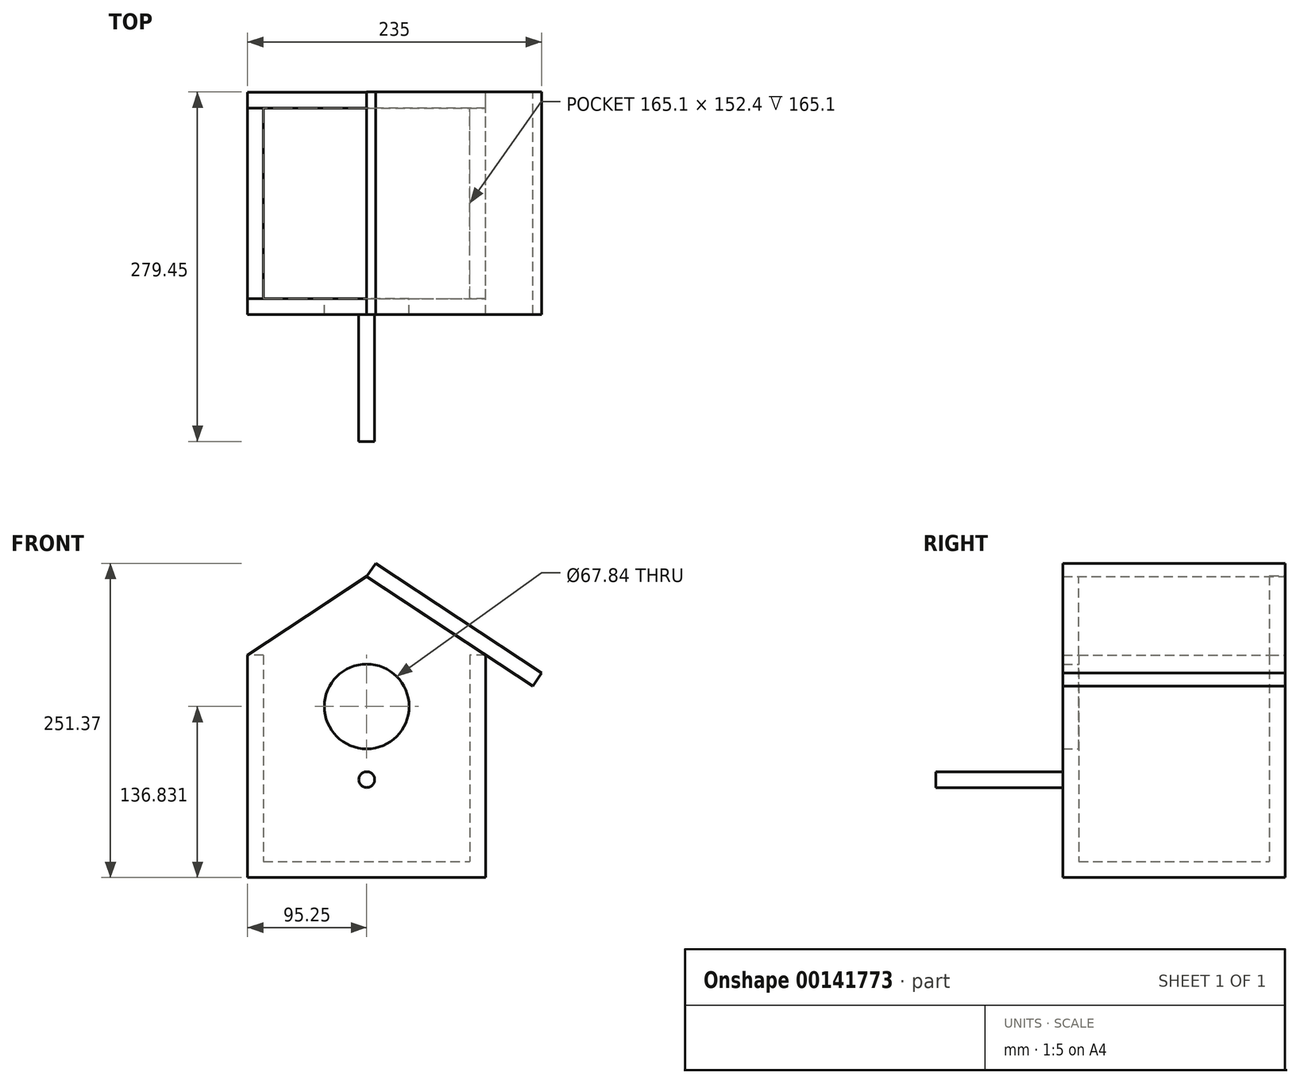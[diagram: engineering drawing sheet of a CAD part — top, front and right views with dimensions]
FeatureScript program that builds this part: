
annotation { "Feature Type Name" : "Feature", "Feature Type Description" : "" }
export const myFeature = defineFeature(function(context is Context, id is Id, definition is map)
    precondition{}
    {
        {
            var Q0;
            Q0=qCreatedBy(makeId("Front.planeOp"),FACE);
            var sketch = newSketch(context, id + "F0", { "sketchPlane" : qUnion([Q0])});
            skLineSegment(sketch, "E0.bottom", {"start": v(-82.55, 82.55) * mm, "end": v(82.55, 82.55) * mm});
            skLineSegment(sketch, "E0.top", {"start": v(-82.55, -82.55) * mm, "end": v(82.55, -82.55) * mm});
            skLineSegment(sketch, "E0.left", {"start": v(-82.55, 82.55) * mm, "end": v(-82.55, -82.55) * mm});
            skLineSegment(sketch, "E0.right", {"start": v(82.55, 82.55) * mm, "end": v(82.55, -82.55) * mm});
            skPoint(sketch, "E0.middle", {"position": v(0, 0) * mm});
            skLineSegment(sketch, "E1", {"start": v(0, 0) * mm, "end": v(0, 145.53) * mm});
            skLineSegment(sketch, "E2", {"start": v(0, 145.53) * mm, "end": v(82.55, 82.55) * mm});
            skLineSegment(sketch, "E3", {"start": v(0, 145.53) * mm, "end": v(-82.55, 82.55) * mm});
            skCircle(sketch, "E4", {"center": v(0, 41.58) * mm, "radius": 33.92 * mm});
            skCircle(sketch, "E5", {"center": v(0, -25.65) * mm, "radius": 12.62 * mm});
            skSolve(sketch);
        }
        {
            var Q0;
            Q0=makeQuery(id+"F0.imprint","IMPRINT",FACE,{"disambiguationData":[TD([[makeQuery(id+"F0.imprint","IMPRINT",EDGE,{"derivedFrom":sQuery(id+"F0.wireOp",EDGE,"E0.top")}),1.0]])]});
            var Q1;
            {var subQ0=sQuery(id+"F0.wireOp",EDGE,"E3");Q1=makeQuery(id+"F0.imprint","IMPRINT",FACE,{"disambiguationData":[TD([[makeQuery(id+"F0.imprint","IMPRINT",EDGE,{"derivedFrom":subQ0}),1.0]])]});}
            var Q2;
            {var subQ0=sQuery(id+"F0.wireOp",EDGE,"E2");Q2=makeQuery(id+"F0.imprint","IMPRINT",FACE,{"disambiguationData":[TD([[makeQuery(id+"F0.imprint","IMPRINT",EDGE,{"derivedFrom":subQ0}),-1.0]])]});}
            var Q3;
            Q3=makeQuery(id+"F0.imprint","IMPRINT",FACE,{"disambiguationData":[TD([[makeQuery(id+"F0.imprint","IMPRINT",EDGE,{"derivedFrom":sQuery(id+"F0.wireOp",EDGE,"E5")}),1.0]])]});
            extrude(context, id + "F1", {"entities" : qUnion([Q0, Q1, Q2, Q3]), "depth" : 12.7 * mm});
        }
        {
            var Q0;
            Q0=makeQuery(id+"F1.opExtrude","CAP_FACE",FACE,{"disambiguationData":[OSD([sQuery(id+"F0.wireOp",EDGE,"E0.top"),sQuery(id+"F0.wireOp",EDGE,"E0.left"),sQuery(id+"F0.wireOp",EDGE,"E0.right"),sQuery(id+"F0.wireOp",EDGE,"E2"),sQuery(id+"F0.wireOp",EDGE,"E3"),sQuery(id+"F0.wireOp",EDGE,"E4")])],"isStart":false});
            var sketch = newSketch(context, id + "F2", { "sketchPlane" : qUnion([Q0])});
            skCircle(sketch, "E6", {"center": v(0, -16.87) * mm, "radius": 6.35 * mm});
            skSolve(sketch);
        }
        {
            var Q0;
            Q0 = qSketchRegion(id + "F2", true);
            extrude(context, id + "F3", {"entities" : qUnion([Q0]), "depth" : 101.6 * mm});
        }
        {
            var Q0;
            Q0=makeQuery(id+"F1.opExtrude","SWEPT_FACE",FACE,{"disambiguationData":[OSD([sQuery(id+"F0.wireOp",EDGE,"E0.right")])]});
            var sketch = newSketch(context, id + "F4", { "sketchPlane" : qUnion([Q0])});
            skLineSegment(sketch, "E7.bottom", {"start": v(-12.7, 82.55) * mm, "end": v(152.4, 82.55) * mm});
            skLineSegment(sketch, "E7.top", {"start": v(-12.7, -82.55) * mm, "end": v(152.4, -82.55) * mm});
            skLineSegment(sketch, "E7.left", {"start": v(-12.7, 82.55) * mm, "end": v(-12.7, -82.55) * mm});
            skLineSegment(sketch, "E7.right", {"start": v(152.4, 82.55) * mm, "end": v(152.4, -82.55) * mm});
            skSolve(sketch);
        }
        {
            var Q0;
            Q0 = qSketchRegion(id + "F4", true);
            extrude(context, id + "F5", {"entities" : qUnion([Q0]), "operationType" : NewBodyOperationType.ADD, "depth" : 12.7 * mm});
        }
        {
            var Q0;
            Q0=makeQuery(id+"F1.opExtrude","SWEPT_FACE",FACE,{"disambiguationData":[OSD([sQuery(id+"F0.wireOp",EDGE,"E0.left")])]});
            var sketch = newSketch(context, id + "F6", { "sketchPlane" : qUnion([Q0])});
            skLineSegment(sketch, "E8.bottom", {"start": v(12.7, 82.55) * mm, "end": v(-152.4, 82.55) * mm});
            skLineSegment(sketch, "E8.top", {"start": v(12.7, -82.55) * mm, "end": v(-152.4, -82.55) * mm});
            skLineSegment(sketch, "E8.left", {"start": v(12.7, 82.55) * mm, "end": v(12.7, -82.55) * mm});
            skLineSegment(sketch, "E8.right", {"start": v(-152.4, 82.55) * mm, "end": v(-152.4, -82.55) * mm});
            skSolve(sketch);
        }
        {
            var Q0;
            Q0 = qSketchRegion(id + "F6", true);
            extrude(context, id + "F7", {"entities" : qUnion([Q0]), "operationType" : NewBodyOperationType.ADD, "depth" : 12.7 * mm});
        }
        {
            var Q0;
            Q0=makeQuery(id+"F5.opExtrude","SWEPT_FACE",FACE,{"disambiguationData":[OSD([sQuery(id+"F4.wireOp",EDGE,"E7.right")])]});
            var sketch = newSketch(context, id + "F8", { "sketchPlane" : qUnion([Q0])});
            skLineSegment(sketch, "E9.bottom", {"start": v(-95.25, 82.55) * mm, "end": v(95.25, 82.55) * mm});
            skLineSegment(sketch, "E9.top", {"start": v(-95.25, -82.55) * mm, "end": v(95.25, -82.55) * mm});
            skLineSegment(sketch, "E9.left", {"start": v(-95.25, 82.55) * mm, "end": v(-95.25, -82.55) * mm});
            skLineSegment(sketch, "E9.right", {"start": v(95.25, 82.55) * mm, "end": v(95.25, -82.55) * mm});
            skSolve(sketch);
        }
        {
            var Q0;
            Q0 = qSketchRegion(id + "F8", true);
            extrude(context, id + "F9", {"entities" : qUnion([Q0]), "operationType" : NewBodyOperationType.ADD, "depth" : 12.7 * mm});
        }
        {
            var Q0;
            Q0=makeQuery(id+"F7.boolean.opBoolean","MERGE",FACE,{"derivedFrom":[makeQuery(id+"F5.boolean.opBoolean","MERGE",FACE,{"derivedFrom":[makeQuery(id+"F1.opExtrude","CAP_FACE",FACE,{"disambiguationData":[OSD([sQuery(id+"F0.wireOp",EDGE,"E0.top"),sQuery(id+"F0.wireOp",EDGE,"E0.left"),sQuery(id+"F0.wireOp",EDGE,"E0.right"),sQuery(id+"F0.wireOp",EDGE,"E2"),sQuery(id+"F0.wireOp",EDGE,"E3"),sQuery(id+"F0.wireOp",EDGE,"E4")])],"isStart":false}),makeQuery(id+"F5.opExtrude","SWEPT_FACE",FACE,{"disambiguationData":[OSD([sQuery(id+"F4.wireOp",EDGE,"E7.left")])]})]}),makeQuery(id+"F7.opExtrude","SWEPT_FACE",FACE,{"disambiguationData":[OSD([sQuery(id+"F6.wireOp",EDGE,"E8.left")])]})]});
            var sketch = newSketch(context, id + "F10", { "sketchPlane" : qUnion([Q0])});
            skLineSegment(sketch, "E10", {"start": v(0, 145.53) * mm, "end": v(95.25, 82.55) * mm});
            skLineSegment(sketch, "E11", {"start": v(95.25, 82.55) * mm, "end": v(82.55, 82.55) * mm});
            skLineSegment(sketch, "E12", {"start": v(82.55, 82.55) * mm, "end": v(0, 145.53) * mm});
            skLineSegment(sketch, "E13", {"start": v(-82.55, 82.55) * mm, "end": v(-95.25, 82.55) * mm});
            skLineSegment(sketch, "E14", {"start": v(-95.25, 82.55) * mm, "end": v(0, 145.53) * mm});
            skSolve(sketch);
        }
        {
            var Q0;
            Q0 = qSketchRegion(id + "F10", true);
            extrude(context, id + "F11", {"entities" : qUnion([Q0]), "oppositeDirection" : true, "depth" : 12.7 * mm});
        }
        {
            var Q0;
            Q0=makeQuery(id+"F7.boolean.opBoolean","MERGE",FACE,{"derivedFrom":[makeQuery(id+"F5.boolean.opBoolean","MERGE",FACE,{"derivedFrom":[makeQuery(id+"F1.opExtrude","CAP_FACE",FACE,{"disambiguationData":[OSD([sQuery(id+"F0.wireOp",EDGE,"E0.top"),sQuery(id+"F0.wireOp",EDGE,"E0.left"),sQuery(id+"F0.wireOp",EDGE,"E0.right"),sQuery(id+"F0.wireOp",EDGE,"E2"),sQuery(id+"F0.wireOp",EDGE,"E3"),sQuery(id+"F0.wireOp",EDGE,"E4")])],"isStart":false}),makeQuery(id+"F5.opExtrude","SWEPT_FACE",FACE,{"disambiguationData":[OSD([sQuery(id+"F4.wireOp",EDGE,"E7.left")])]})]}),makeQuery(id+"F7.opExtrude","SWEPT_FACE",FACE,{"disambiguationData":[OSD([sQuery(id+"F6.wireOp",EDGE,"E8.left")])]})]});
            var sketch = newSketch(context, id + "F12", { "sketchPlane" : qUnion([Q0])});
            skLineSegment(sketch, "E15", {"start": v(0, 145.53) * mm, "end": v(-82.55, 82.55) * mm});
            skLineSegment(sketch, "E16", {"start": v(-82.55, 82.55) * mm, "end": v(-95.25, 82.55) * mm});
            skLineSegment(sketch, "E17", {"start": v(-95.25, 82.55) * mm, "end": v(0, 145.53) * mm});
            skSolve(sketch);
        }
        {
            var Q0;
            Q0 = qSketchRegion(id + "F12", true);
            extrude(context, id + "F13", {"entities" : qUnion([Q0]), "operationType" : NewBodyOperationType.ADD, "oppositeDirection" : true, "depth" : 12.7 * mm});
        }
        {
            var Q0;
            Q0=makeQuery(id+"F9.opExtrude","CAP_FACE",FACE,{"disambiguationData":[OSD([sQuery(id+"F8.wireOp",EDGE,"E9.bottom"),sQuery(id+"F8.wireOp",EDGE,"E9.top"),sQuery(id+"F8.wireOp",EDGE,"E9.left"),sQuery(id+"F8.wireOp",EDGE,"E9.right")])],"isStart":false});
            var sketch = newSketch(context, id + "F14", { "sketchPlane" : qUnion([Q0])});
            skLineSegment(sketch, "E18", {"start": v(0, 82.55) * mm, "end": v(0, 146.05) * mm});
            skPoint(sketch, "E18.endSnap0", {"position": v(0, 82.55) * mm});
            skLineSegment(sketch, "E19", {"start": v(0, 146.05) * mm, "end": v(-95.25, 82.55) * mm});
            skLineSegment(sketch, "E20", {"start": v(-95.25, 82.55) * mm, "end": v(95.25, 82.55) * mm});
            skLineSegment(sketch, "E21", {"start": v(95.25, 82.55) * mm, "end": v(0, 146.05) * mm});
            skSolve(sketch);
        }
        {
            var Q0;
            Q0 = qSketchRegion(id + "F14", true);
            extrude(context, id + "F15", {"entities" : qUnion([Q0]), "operationType" : NewBodyOperationType.ADD, "oppositeDirection" : true, "depth" : 12.7 * mm});
        }
        {
            var Q0;
            Q0=makeQuery(id+"F11.opExtrude","SWEPT_FACE",FACE,{"disambiguationData":[OSD([sQuery(id+"F10.wireOp",EDGE,"E10")])]});
            var sketch = newSketch(context, id + "F16", { "sketchPlane" : qUnion([Q0])});
            skLineSegment(sketch, "E22", {"start": v(-80.26, -12.7) * mm, "end": v(-80.26, 165.15) * mm});
            skLineSegment(sketch, "E23", {"start": v(-80.26, 165.15) * mm, "end": v(33.5, 165.15) * mm});
            skLineSegment(sketch, "E24", {"start": v(33.93, -12.7) * mm, "end": v(-80.26, -12.7) * mm});
            skLineSegment(sketch, "E25", {"start": v(33.93, -12.7) * mm, "end": v(79.77, -12.7) * mm});
            skLineSegment(sketch, "E26.bottom", {"start": v(-80.26, -12.7) * mm, "end": v(78.88, -12.7) * mm});
            skLineSegment(sketch, "E26.top", {"start": v(-80.26, 165.15) * mm, "end": v(78.88, 165.15) * mm});
            skLineSegment(sketch, "E26.right", {"start": v(78.88, -12.7) * mm, "end": v(78.88, 165.15) * mm});
            skSolve(sketch);
        }
        {
            var Q0;
            Q0 = qSketchRegion(id + "F16", true);
            extrude(context, id + "F17", {"entities" : qUnion([Q0]), "depth" : 12.7 * mm});
        }
        {
            var Q0;
            Q0=makeQuery(id+"F9.boolean.opBoolean","MERGE",FACE,{"derivedFrom":[makeQuery(id+"F7.boolean.opBoolean","MERGE",FACE,{"derivedFrom":[makeQuery(id+"F5.boolean.opBoolean","MERGE",FACE,{"derivedFrom":[makeQuery(id+"F1.opExtrude","SWEPT_FACE",FACE,{"disambiguationData":[OSD([sQuery(id+"F0.wireOp",EDGE,"E0.top")])]}),makeQuery(id+"F5.opExtrude","SWEPT_FACE",FACE,{"disambiguationData":[OSD([sQuery(id+"F4.wireOp",EDGE,"E7.top")])]})]}),makeQuery(id+"F7.opExtrude","SWEPT_FACE",FACE,{"disambiguationData":[OSD([sQuery(id+"F6.wireOp",EDGE,"E8.top")])]})]}),makeQuery(id+"F9.opExtrude","SWEPT_FACE",FACE,{"disambiguationData":[OSD([sQuery(id+"F8.wireOp",EDGE,"E9.top")])]})]});
            var sketch = newSketch(context, id + "F18", { "sketchPlane" : qUnion([Q0])});
            skLineSegment(sketch, "E27.bottom", {"start": v(-95.25, 12.7) * mm, "end": v(95.25, 12.7) * mm});
            skLineSegment(sketch, "E27.top", {"start": v(-95.25, -165.1) * mm, "end": v(95.25, -165.1) * mm});
            skLineSegment(sketch, "E27.left", {"start": v(-95.25, 12.7) * mm, "end": v(-95.25, -165.1) * mm});
            skLineSegment(sketch, "E27.right", {"start": v(95.25, 12.7) * mm, "end": v(95.25, -165.1) * mm});
            skSolve(sketch);
        }
        {
            var Q0;
            Q0 = qSketchRegion(id + "F18", true);
            extrude(context, id + "F19", {"entities" : qUnion([Q0]), "operationType" : NewBodyOperationType.ADD, "depth" : 12.7 * mm});
        }
    });
